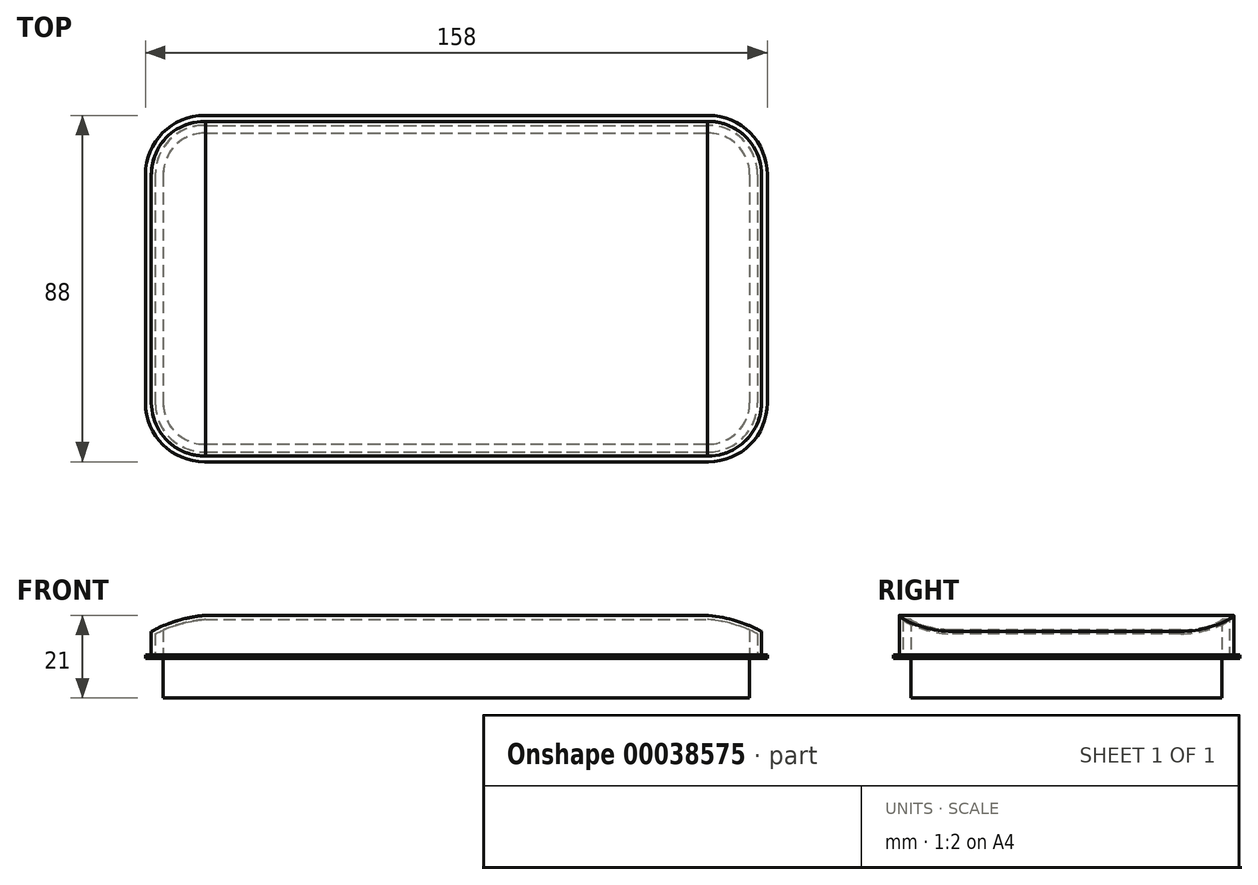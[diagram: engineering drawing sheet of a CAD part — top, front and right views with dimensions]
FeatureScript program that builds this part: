
annotation { "Feature Type Name" : "Feature", "Feature Type Description" : "" }
export const myFeature = defineFeature(function(context is Context, id is Id, definition is map)
    precondition{}
    {
        {
            var Q0;
            Q0=qCreatedBy(makeId("Top.planeOp"),FACE);
            var sketch = newSketch(context, id + "F0", { "sketchPlane" : qUnion([Q0])});
            skLineSegment(sketch, "E0.bottom", {"start": v(15, 0) * mm, "end": v(143, 0) * mm});
            skLineSegment(sketch, "E0.top", {"start": v(15, 88) * mm, "end": v(143, 88) * mm});
            skLineSegment(sketch, "E0.left", {"start": v(0, 15) * mm, "end": v(0, 73) * mm});
            skLineSegment(sketch, "E0.right", {"start": v(158, 15) * mm, "end": v(158, 73) * mm});
            skLineSegment(sketch, "E1.bottom", {"start": v(15, 86.5) * mm, "end": v(143, 86.5) * mm});
            skLineSegment(sketch, "E1.top", {"start": v(15, 1.5) * mm, "end": v(143, 1.5) * mm});
            skLineSegment(sketch, "E1.left", {"start": v(1.5, 73) * mm, "end": v(1.5, 15) * mm});
            skLineSegment(sketch, "E1.right", {"start": v(156.5, 73) * mm, "end": v(156.5, 15) * mm});
            skPoint(sketch, "E2", {"position": v(143, 73) * mm});
            skArc(sketch, "E3", {"start": v(158, 73) * mm, "mid": v(153.6, 83.6) * mm, "end": v(143, 88) * mm});
            skArc(sketch, "E4", {"start": v(156.5, 73) * mm, "mid": v(152.55, 82.55) * mm, "end": v(143, 86.5) * mm});
            skPoint(sketch, "E5", {"position": v(15, 73) * mm});
            skPoint(sketch, "E6", {"position": v(15, 15) * mm});
            skPoint(sketch, "E7", {"position": v(143, 15) * mm});
            skArc(sketch, "E8", {"start": v(15, 88) * mm, "mid": v(4.4, 83.6) * mm, "end": v(0, 73) * mm});
            skArc(sketch, "E9", {"start": v(15, 86.5) * mm, "mid": v(5.45, 82.55) * mm, "end": v(1.5, 73) * mm});
            skArc(sketch, "E10", {"start": v(1.5, 15) * mm, "mid": v(5.45, 5.45) * mm, "end": v(15, 1.5) * mm});
            skArc(sketch, "E11", {"start": v(0, 15) * mm, "mid": v(4.4, 4.4) * mm, "end": v(15, 0) * mm});
            skArc(sketch, "E12", {"start": v(143, 1.5) * mm, "mid": v(152.55, 5.45) * mm, "end": v(156.5, 15) * mm});
            skArc(sketch, "E13", {"start": v(143, 0) * mm, "mid": v(153.6, 4.4) * mm, "end": v(158, 15) * mm});
            skSolve(sketch);
        }
        {
            var Q0;
            Q0=makeQuery(id+"F0.imprint","IMPRINT",FACE,{"disambiguationData":[TD([[makeQuery(id+"F0.imprint","IMPRINT",EDGE,{"derivedFrom":sQuery(id+"F0.wireOp",EDGE,"E0.bottom")}),1.0]])]});
            extrude(context, id + "F1", {"entities" : qUnion([Q0]), "depth" : 1 * mm});
        }
        {
            var Q0;
            Q0=makeQuery(id+"F0.imprint","IMPRINT",FACE,{"disambiguationData":[TD([[makeQuery(id+"F0.imprint","IMPRINT",EDGE,{"derivedFrom":sQuery(id+"F0.wireOp",EDGE,"E1.bottom")}),-1.0]])]});
            extrude(context, id + "F2", {"entities" : qUnion([Q0]), "operationType" : NewBodyOperationType.ADD, "depth" : 11 * mm});
        }
        {
            var Q0;
            Q0=qCreatedBy(makeId("Front.planeOp"),FACE);
            var sketch = newSketch(context, id + "F3", { "sketchPlane" : qUnion([Q0])});
            skLineSegment(sketch, "E14.0", {"start": v(15, 11) * mm, "end": v(143, 11) * mm});
            skLineSegment(sketch, "E15.0", {"start": v(15, 0) * mm, "end": v(143, 0) * mm});
            skLineSegment(sketch, "E16.bottom", {"start": v(0, 11.06) * mm, "end": v(158, 11.06) * mm});
            skLineSegment(sketch, "E16.top", {"start": v(0, 0) * mm, "end": v(158, 0) * mm});
            skLineSegment(sketch, "E17.left", {"start": v(0, 0) * mm, "end": v(0, 11.06) * mm});
            skPoint(sketch, "E18.0", {"position": v(158, 0) * mm});
            skLineSegment(sketch, "E19", {"start": v(158, 0) * mm, "end": v(158, 11.06) * mm});
            skPoint(sketch, "E20", {"position": v(0, 6.06) * mm});
            skPoint(sketch, "E21", {"position": v(16, 11.06) * mm});
            skPoint(sketch, "E22", {"position": v(142, 11.06) * mm});
            skPoint(sketch, "E23", {"position": v(158, 6.06) * mm});
            skPoint(sketch, "E16.right.end.orphan", {"position": v(165.37, 0) * mm});
            skArc(sketch, "E24", {"start": v(158, 6.06) * mm, "mid": v(150.3, 9.53) * mm, "end": v(142, 11.06) * mm});
            skArc(sketch, "E25", {"start": v(16, 11.06) * mm, "mid": v(7.7, 9.53) * mm, "end": v(0, 6.06) * mm});
            skSolve(sketch);
        }
        {
            var Q0;
            {var subQ2=sQuery(id+"F3.wireOp",EDGE,"E16.bottom");var subQ4=sQuery(id+"F3.wireOp",EDGE,"E17.left");var subQ6=makeQuery(id+"F3.imprint","INTERSECT",VERTEX,{"derivedFrom":[subQ2,subQ4]});Q0=makeQuery(id+"F3.imprint","IMPRINT",FACE,{"disambiguationData":[TD([[makeQuery(id+"F3.imprint","IMPRINT",EDGE,{"disambiguationData":[TD([[subQ6,-1.0]])],"derivedFrom":subQ2}),-1.0]])]});}
            var Q1;
            {var subQ2=sQuery(id+"F3.wireOp",EDGE,"E16.bottom");var subQ4=sQuery(id+"F3.wireOp",EDGE,"E19");var subQ6=makeQuery(id+"F3.imprint","INTERSECT",VERTEX,{"derivedFrom":[subQ2,subQ4]});Q1=makeQuery(id+"F3.imprint","IMPRINT",FACE,{"disambiguationData":[TD([[makeQuery(id+"F3.imprint","IMPRINT",EDGE,{"disambiguationData":[TD([[subQ6,1.0]])],"derivedFrom":subQ2}),-1.0]])]});}
            extrude(context, id + "F4", {"entities" : qUnion([Q0, Q1]), "operationType" : NewBodyOperationType.REMOVE, "endBound" : BoundingType.THROUGH_ALL, "oppositeDirection" : true, "depth" : 25 * mm});
        }
        {
            var Q0;
            {var subQ0=sQuery(id+"F0.wireOp",EDGE,"E1.bottom");var subQ1=sQuery(id+"F0.wireOp",EDGE,"E1.top");var subQ2=sQuery(id+"F0.wireOp",EDGE,"E1.left");var subQ3=sQuery(id+"F0.wireOp",EDGE,"E1.right");var subQ4=sQuery(id+"F0.wireOp",EDGE,"E4");var subQ5=sQuery(id+"F0.wireOp",EDGE,"E9");var subQ6=sQuery(id+"F0.wireOp",EDGE,"E10");var subQ7=sQuery(id+"F0.wireOp",EDGE,"E12");Q0=makeQuery(id+"F2.boolean.opBoolean","MERGE",FACE,{"derivedFrom":[makeQuery(id+"F1.opExtrude","CAP_FACE",FACE,{"disambiguationData":[OSD([sQuery(id+"F0.wireOp",EDGE,"E0.bottom"),sQuery(id+"F0.wireOp",EDGE,"E0.top"),sQuery(id+"F0.wireOp",EDGE,"E0.left"),sQuery(id+"F0.wireOp",EDGE,"E0.right"),subQ0,subQ1,subQ2,subQ3,sQuery(id+"F0.wireOp",EDGE,"E3"),subQ4,sQuery(id+"F0.wireOp",EDGE,"E8"),subQ5,subQ6,sQuery(id+"F0.wireOp",EDGE,"E11"),subQ7,sQuery(id+"F0.wireOp",EDGE,"E13")])],"isStart":true}),makeQuery(id+"F2.opExtrude","CAP_FACE",FACE,{"disambiguationData":[OSD([subQ0,subQ1,subQ2,subQ3,subQ4,subQ5,subQ6,subQ7])],"isStart":true})]});}
            shell(context, id + "F5", {"entities" : qUnion([Q0]), "thickness" : 1 * mm});
        }
        {
            var Q0;
            Q0=qCreatedBy(makeId("Top.planeOp"),FACE);
            var sketch = newSketch(context, id + "F6", { "sketchPlane" : qUnion([Q0])});
            skLineSegment(sketch, "E26.0", {"start": v(2.5, 73) * mm, "end": v(2.5, 15) * mm});
            skLineSegment(sketch, "E27.0", {"start": v(15, 2.5) * mm, "end": v(143, 2.5) * mm});
            skArc(sketch, "E28.0", {"start": v(2.5, 15) * mm, "mid": v(6.16, 6.16) * mm, "end": v(15, 2.5) * mm});
            skPoint(sketch, "E29.0", {"position": v(143, 15) * mm});
            skArc(sketch, "E30.0", {"start": v(143, 2.5) * mm, "mid": v(151.84, 6.16) * mm, "end": v(155.5, 15) * mm});
            skLineSegment(sketch, "E31.0", {"start": v(155.5, 73) * mm, "end": v(155.5, 15) * mm});
            skPoint(sketch, "E32.0", {"position": v(143, 73) * mm});
            skLineSegment(sketch, "E33.0", {"start": v(15, 85.5) * mm, "end": v(143, 85.5) * mm});
            skPoint(sketch, "E34.0", {"position": v(15, 73) * mm});
            skLineSegment(sketch, "E35.top", {"start": v(15, 83.5) * mm, "end": v(143, 83.5) * mm});
            skLineSegment(sketch, "E35.right", {"start": v(153.5, 15) * mm, "end": v(153.5, 73) * mm});
            skArc(sketch, "E36", {"start": v(4.5, 14.98) * mm, "mid": v(7.58, 7.58) * mm, "end": v(14.98, 4.5) * mm});
            skArc(sketch, "E37", {"start": v(143, 4.5) * mm, "mid": v(150.42, 7.58) * mm, "end": v(153.5, 15) * mm});
            skArc(sketch, "E38", {"start": v(15, 83.5) * mm, "mid": v(7.58, 80.42) * mm, "end": v(4.5, 73) * mm});
            skArc(sketch, "E39", {"start": v(153.5, 73) * mm, "mid": v(150.42, 80.42) * mm, "end": v(143, 83.5) * mm});
            skLineSegment(sketch, "E40.trimOffspring", {"start": v(14.98, 4.5) * mm, "end": v(143, 4.5) * mm});
            skLineSegment(sketch, "E41.trimOffspring", {"start": v(4.5, 14.98) * mm, "end": v(4.5, 73) * mm});
            skSolve(sketch);
        }
        {
            var Q0;
            Q0=makeQuery(id+"F6.imprint","IMPRINT",FACE,{"disambiguationData":[TD([[makeQuery(id+"F6.imprint","IMPRINT",EDGE,{"derivedFrom":sQuery(id+"F6.wireOp",EDGE,"E35.top")}),-1.0]])]});
            extrude(context, id + "F7", {"entities" : qUnion([Q0]), "operationType" : NewBodyOperationType.ADD, "endBound" : BoundingType.UP_TO_NEXT, "depth" : 25 * mm});
        }
        {
            var Q0;
            Q0 = qSketchRegion(id + "F6", true);
            extrude(context, id + "F8", {"entities" : qUnion([Q0]), "operationType" : NewBodyOperationType.ADD, "oppositeDirection" : true, "depth" : 10 * mm});
        }
    });
